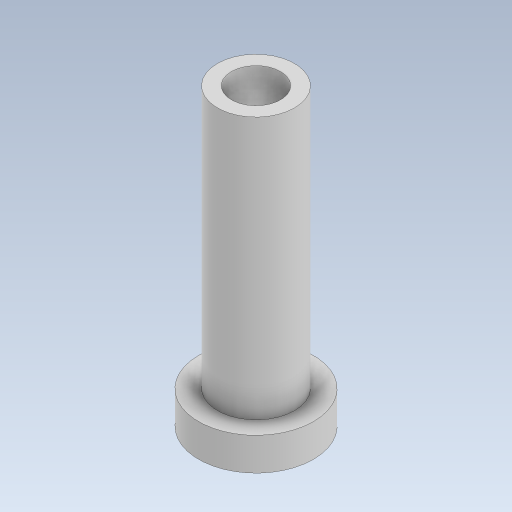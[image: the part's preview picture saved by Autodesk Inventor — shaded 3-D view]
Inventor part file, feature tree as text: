
AUTODESK INVENTOR PART (.ipt)
format: ipt  version: 2023.5 (Build 275446000, 446)  size: 239,616 bytes
history: native  units: mm
features: extrude x2, sketch x1
ambient origin geometry x8: Origin, YZ Plane, XZ Plane, XY Plane, X Axis, Y Axis, Z Axis, Center Point
bodies: Solid1 (feature_tree)
feature tree (3):
  sketch  "Sketch1"  dims[d0=4.7mm d1=7.0mm d2=3.0mm d3=2.0mm d4=0.0mm d5=18.0mm d6=0.0mm]
  extrude  "Extrusion1"  Depth=18.0mm
  extrude  "Extrusion2"  Depth=18.0mm
